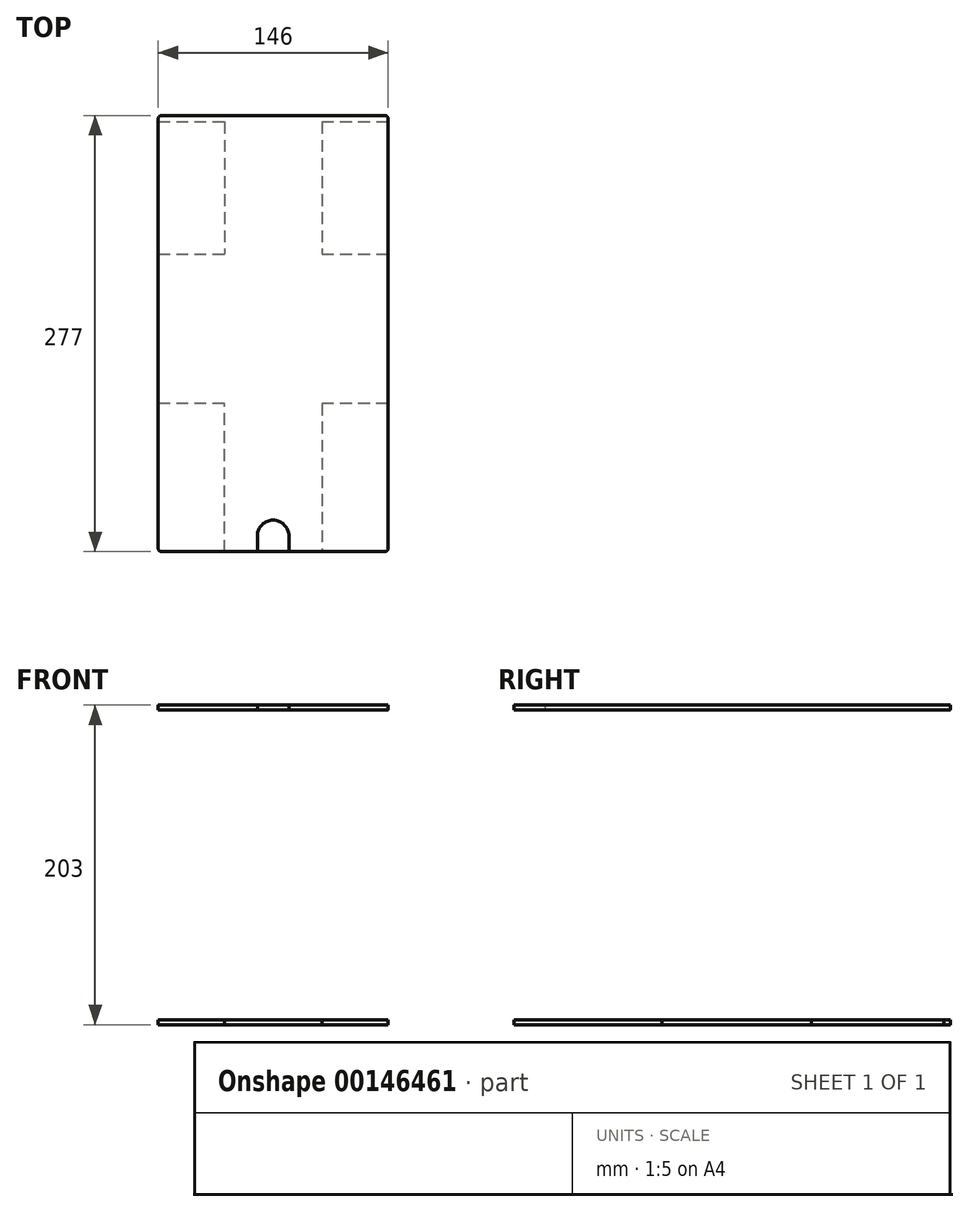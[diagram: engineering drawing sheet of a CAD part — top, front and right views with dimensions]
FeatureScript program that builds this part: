
annotation { "Feature Type Name" : "Feature", "Feature Type Description" : "" }
export const myFeature = defineFeature(function(context is Context, id is Id, definition is map)
    precondition{}
    {
        {
            var Q0;
            Q0=qCreatedBy(makeId("Top.planeOp"),FACE);
            var sketch = newSketch(context, id + "F0", { "sketchPlane" : qUnion([Q0])});
            skLineSegment(sketch, "E0.bottom", {"start": v(-73, 138.5) * mm, "end": v(73, 138.5) * mm});
            skLineSegment(sketch, "E0.top", {"start": v(-73, -138.5) * mm, "end": v(73, -138.5) * mm});
            skLineSegment(sketch, "E0.left", {"start": v(-73, 138.5) * mm, "end": v(-73, -138.5) * mm});
            skLineSegment(sketch, "E0.right", {"start": v(73, 138.5) * mm, "end": v(73, -138.5) * mm});
            skPoint(sketch, "E0.middle", {"position": v(0, 0) * mm});
            skSolve(sketch);
        }
        {
            var Q0;
            Q0=makeQuery(id+"F0.imprint","IMPRINT",FACE,{"disambiguationData":[TD([[makeQuery(id+"F0.imprint","IMPRINT",EDGE,{"derivedFrom":sQuery(id+"F0.wireOp",EDGE,"E0.bottom")}),-1.0]])]});
            extrude(context, id + "F1", {"entities" : qUnion([Q0]), "depth" : 3 * mm, "symmetric" : true});
        }
        {
            var Q0;
            Q0=makeQuery(id+"F1.opExtrude","SWEPT_EDGE",EDGE,{"disambiguationData":[OSD([sQuery(id+"F0.wireOp",EDGE,"E0.bottom"),sQuery(id+"F0.wireOp",EDGE,"E0.left")])]});
            var Q1;
            Q1=makeQuery(id+"F1.opExtrude","SWEPT_EDGE",EDGE,{"disambiguationData":[OSD([sQuery(id+"F0.wireOp",EDGE,"E0.bottom"),sQuery(id+"F0.wireOp",EDGE,"E0.right")])]});
            var Q2;
            Q2=makeQuery(id+"F1.opExtrude","SWEPT_EDGE",EDGE,{"disambiguationData":[OSD([sQuery(id+"F0.wireOp",EDGE,"E0.top"),sQuery(id+"F0.wireOp",EDGE,"E0.right")])]});
            var Q3;
            Q3=makeQuery(id+"F1.opExtrude","SWEPT_EDGE",EDGE,{"disambiguationData":[OSD([sQuery(id+"F0.wireOp",EDGE,"E0.top"),sQuery(id+"F0.wireOp",EDGE,"E0.left")])]});
            fillet(context, id + "F2", {"entities" : qUnion([Q0, Q1, Q2, Q3]), "radius" : 2 * mm, "tangentPropagation" : true, "allowEdgeOverflow" : false});
        }
        {
            var Q0;
            Q0=makeQuery(id+"F1.opExtrude","CAP_FACE",FACE,{"disambiguationData":[OSD([sQuery(id+"F0.wireOp",EDGE,"E0.bottom"),sQuery(id+"F0.wireOp",EDGE,"E0.top"),sQuery(id+"F0.wireOp",EDGE,"E0.left"),sQuery(id+"F0.wireOp",EDGE,"E0.right")])],"isStart":false});
            var sketch = newSketch(context, id + "F3", { "sketchPlane" : qUnion([Q0])});
            skLineSegment(sketch, "E1", {"start": v(-10, -128.5) * mm, "end": v(-10, -138.5) * mm});
            skLineSegment(sketch, "E2", {"start": v(-10, -138.5) * mm, "end": v(10, -138.5) * mm});
            skLineSegment(sketch, "E3", {"start": v(10, -138.5) * mm, "end": v(10, -128.5) * mm});
            skArc(sketch, "E4", {"start": v(-10, -128.5) * mm, "mid": v(0, -118.5) * mm, "end": v(10, -128.5) * mm});
            skLineSegment(sketch, "E5", {"start": v(0, -128.5) * mm, "end": v(0, 0) * mm, "construction": true});
            skSolve(sketch);
        }
        {
            var Q0;
            Q0=makeQuery(id+"F1.opExtrude","CAP_FACE",FACE,{"disambiguationData":[OSD([sQuery(id+"F0.wireOp",EDGE,"E0.bottom"),sQuery(id+"F0.wireOp",EDGE,"E0.top"),sQuery(id+"F0.wireOp",EDGE,"E0.left"),sQuery(id+"F0.wireOp",EDGE,"E0.right")])],"isStart":false});
            var sketch = newSketch(context, id + "F4", { "sketchPlane" : qUnion([Q0])});
            skCircle(sketch, "E6", {"center": v(0, -128.5) * mm, "radius": 7.5 * mm});
            skSolve(sketch);
        }
        {
            var Q0;
            Q0=makeQuery(id+"F4.imprint","IMPRINT",FACE,{"disambiguationData":[TD([[makeQuery(id+"F4.imprint","IMPRINT",EDGE,{"derivedFrom":sQuery(id+"F4.wireOp",EDGE,"E6")}),1.0]])]});
            var Q1;
            Q1=sQuery(id+"F4.wireOp",EDGE,"E6");
            extrude(context, id + "F5", {"entities" : qUnion([Q0]), "surfaceEntities" : qUnion([Q1]), "oppositeDirection" : true, "depth" : 100 * mm});
        }
        {
            var Q0;
            Q0=makeQuery(id+"F5.opExtrude","CAP_FACE",FACE,{"disambiguationData":[OSD([sQuery(id+"F4.wireOp",EDGE,"E6")])],"isStart":true});
            shell(context, id + "F6", {"entities" : qUnion([Q0]), "thickness" : 1.5 * mm});
        }
        {
            var Q0;
            Q0=makeQuery(id+"F5.opExtrude","CAP_FACE",FACE,{"disambiguationData":[OSD([sQuery(id+"F4.wireOp",EDGE,"E6")])],"isStart":true});
            var sketch = newSketch(context, id + "F7", { "sketchPlane" : qUnion([Q0])});
            skCircle(sketch, "E7.0", {"center": v(0, -128.5) * mm, "radius": 6 * mm});
            skSolve(sketch);
        }
        {
            var Q0;
            Q0=qCreatedBy(makeId("Top.planeOp"),FACE);
            cPlane(context, id + "F8", {"entities" : qUnion([Q0]), "cplaneType" : CPlaneType.OFFSET, "offset" : 100 * mm, "width" : 150 * mm, "height" : 150 * mm});
        }
        {
            var Q0;
            Q0=makeQuery(id+"F1.opExtrude","SWEPT_BODY",BODY,{"disambiguationData":[OSD([sQuery(id+"F0.wireOp",EDGE,"E0.bottom"),sQuery(id+"F0.wireOp",EDGE,"E0.top"),sQuery(id+"F0.wireOp",EDGE,"E0.left"),sQuery(id+"F0.wireOp",EDGE,"E0.right")])]});
            var Q1;
            Q1=qCreatedBy(id+"F8.planeOp",FACE);
            mirror(context, id + "F9", {"entities" : qUnion([Q0]), "mirrorPlane" : qUnion([Q1])});
        }
        {
            var Q0;
            Q0=makeQuery(id+"F9.opPattern","COPY",FACE,{"derivedFrom":makeQuery(id+"F1.opExtrude","CAP_FACE",FACE,{"disambiguationData":[OSD([sQuery(id+"F0.wireOp",EDGE,"E0.bottom"),sQuery(id+"F0.wireOp",EDGE,"E0.top"),sQuery(id+"F0.wireOp",EDGE,"E0.left"),sQuery(id+"F0.wireOp",EDGE,"E0.right")])],"isStart":true}),"instanceName":"1"});
            var sketch = newSketch(context, id + "F10", { "sketchPlane" : qUnion([Q0])});
            skSolve(sketch);
        }
        {
            var Q0;
            {var subQ3=sQuery(id+"F0.wireOp",EDGE,"E0.bottom");Q0=makeQuery(id+"F10.imprint","IMPRINT",FACE,{"disambiguationData":[TD([[makeQuery(id+"F10.imprint","IMPRINT",EDGE,{"derivedFrom":makeQuery(id+"F9.opPattern","COPY",EDGE,{"derivedFrom":makeQuery(id+"F1.opExtrude","CAP_EDGE",EDGE,{"disambiguationData":[OSD([subQ3])],"isStart":true}),"instanceName":"1"})}),-1.0]])]});}
            var sketch = newSketch(context, id + "F11", { "sketchPlane" : qUnion([Q0])});
            skLineSegment(sketch, "E8", {"start": v(-10, -138.54) * mm, "end": v(-10, -128.54) * mm});
            skLineSegment(sketch, "E9", {"start": v(10, -138.54) * mm, "end": v(10, -128.54) * mm});
            skArc(sketch, "E10", {"start": v(10, -128.54) * mm, "mid": v(0, -118.54) * mm, "end": v(-10, -128.54) * mm});
            skLineSegment(sketch, "E11", {"start": v(-10, -138.54) * mm, "end": v(10, -138.54) * mm});
            skSolve(sketch);
        }
        {
            var Q0;
            Q0 = qSketchRegion(id + "F11", true);
            extrude(context, id + "F12", {"entities" : qUnion([Q0]), "operationType" : NewBodyOperationType.REMOVE, "oppositeDirection" : true, "offsetDistance" : 25 * mm, "depth" : 8 * mm});
        }
        {
            var Q0;
            Q0=makeQuery(id+"F5.opExtrude","SWEPT_BODY",BODY,{"disambiguationData":[OSD([sQuery(id+"F4.wireOp",EDGE,"E6")])]});
            deleteBodies(context, id + "F13", {"entities" : qUnion([Q0])});
        }
        {
            var Q0;
            {var subQ10=sQuery(id+"F3.wireOp",EDGE,"E1");Q0=makeQuery(id+"F3.imprint","IMPRINT",FACE,{"disambiguationData":[TD([[makeQuery(id+"F3.imprint","IMPRINT",EDGE,{"derivedFrom":subQ10}),-1.0]])]});}
            var sketch = newSketch(context, id + "F14", { "sketchPlane" : qUnion([Q0])});
            skLineSegment(sketch, "E12.bottom", {"start": v(31, 138.5) * mm, "end": v(73, 138.5) * mm});
            skLineSegment(sketch, "E12.top", {"start": v(31, 44.5) * mm, "end": v(73, 44.5) * mm});
            skLineSegment(sketch, "E12.left", {"start": v(31, 138.5) * mm, "end": v(31, 44.5) * mm});
            skLineSegment(sketch, "E12.right", {"start": v(73, 138.5) * mm, "end": v(73, 44.5) * mm});
            skSolve(sketch);
        }
        {
            var Q0;
            {var subQ10=sQuery(id+"F3.wireOp",EDGE,"E1");Q0=makeQuery(id+"F3.imprint","IMPRINT",FACE,{"disambiguationData":[TD([[makeQuery(id+"F3.imprint","IMPRINT",EDGE,{"derivedFrom":subQ10}),-1.0]])]});}
            var sketch = newSketch(context, id + "F15", { "sketchPlane" : qUnion([Q0])});
            skLineSegment(sketch, "E13.bottom", {"start": v(73, -44.5) * mm, "end": v(31, -44.5) * mm});
            skLineSegment(sketch, "E13.top", {"start": v(73, -138.5) * mm, "end": v(31, -138.5) * mm});
            skLineSegment(sketch, "E13.left", {"start": v(73, -44.5) * mm, "end": v(73, -138.5) * mm});
            skLineSegment(sketch, "E13.right", {"start": v(31, -44.5) * mm, "end": v(31, -138.5) * mm});
            skLineSegment(sketch, "E14.bottom", {"start": v(-31, -138.5) * mm, "end": v(-73, -138.5) * mm});
            skLineSegment(sketch, "E14.top", {"start": v(-31, -44.5) * mm, "end": v(-73, -44.5) * mm});
            skLineSegment(sketch, "E14.left", {"start": v(-31, -138.5) * mm, "end": v(-31, -44.5) * mm});
            skLineSegment(sketch, "E14.right", {"start": v(-73, -138.5) * mm, "end": v(-73, -44.5) * mm});
            skSolve(sketch);
        }
        {
            var Q0;
            Q0 = qSketchRegion(id + "F15", true);
            extrude(context, id + "F16", {"entities" : qUnion([Q0]), "operationType" : NewBodyOperationType.REMOVE, "oppositeDirection" : true, "depth" : 6 * mm});
        }
        {
            var Q0;
            {var subQ10=sQuery(id+"F3.wireOp",EDGE,"E1");Q0=makeQuery(id+"F3.imprint","IMPRINT",FACE,{"disambiguationData":[TD([[makeQuery(id+"F3.imprint","IMPRINT",EDGE,{"derivedFrom":subQ10}),-1.0]])]});}
            var sketch = newSketch(context, id + "F17", { "sketchPlane" : qUnion([Q0])});
            skLineSegment(sketch, "E15.bottom", {"start": v(-73, 134.5) * mm, "end": v(-31, 134.5) * mm});
            skLineSegment(sketch, "E15.top", {"start": v(-73, 50.5) * mm, "end": v(-31, 50.5) * mm});
            skLineSegment(sketch, "E15.left", {"start": v(-73, 134.5) * mm, "end": v(-73, 50.5) * mm});
            skLineSegment(sketch, "E15.right", {"start": v(-31, 134.5) * mm, "end": v(-31, 50.5) * mm});
            skLineSegment(sketch, "E16.bottom", {"start": v(31, 134.5) * mm, "end": v(73, 134.5) * mm});
            skLineSegment(sketch, "E16.top", {"start": v(31, 50.5) * mm, "end": v(73, 50.5) * mm});
            skLineSegment(sketch, "E16.left", {"start": v(31, 134.5) * mm, "end": v(31, 50.5) * mm});
            skLineSegment(sketch, "E16.right", {"start": v(73, 134.5) * mm, "end": v(73, 50.5) * mm});
            skSolve(sketch);
        }
        {
            var Q0;
            Q0 = qSketchRegion(id + "F17", true);
            extrude(context, id + "F18", {"entities" : qUnion([Q0]), "operationType" : NewBodyOperationType.REMOVE, "oppositeDirection" : true, "depth" : 6 * mm});
        }
    });
